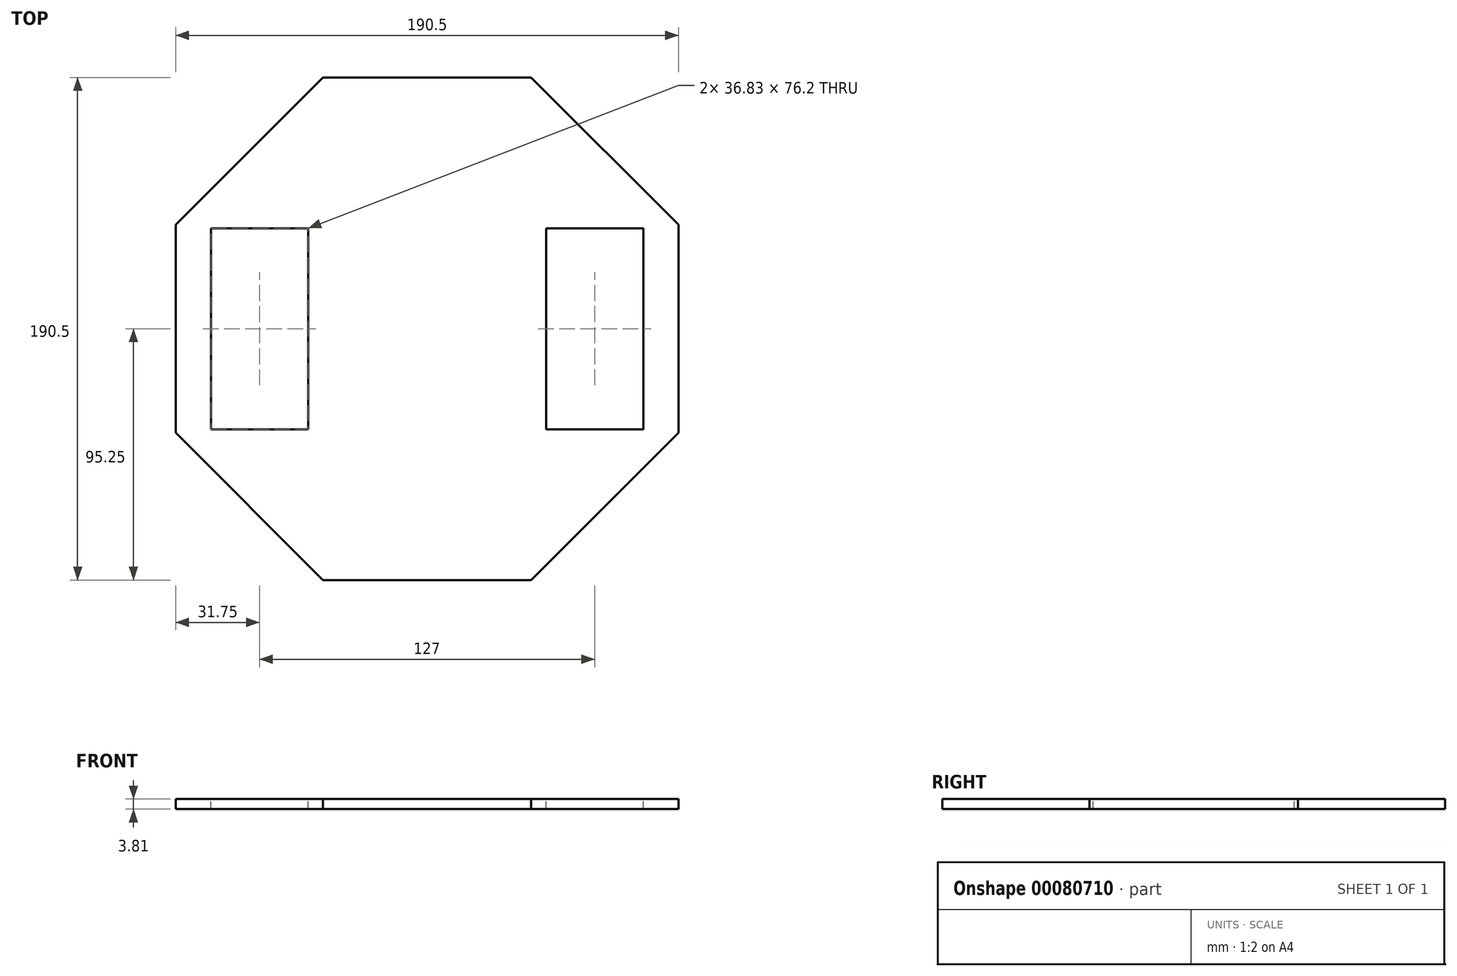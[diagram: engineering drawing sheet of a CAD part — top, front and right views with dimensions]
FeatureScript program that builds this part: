
annotation { "Feature Type Name" : "Feature", "Feature Type Description" : "" }
export const myFeature = defineFeature(function(context is Context, id is Id, definition is map)
    precondition{}
    {
        {
            var Q0;
            Q0=qCreatedBy(makeId("Top.planeOp"),FACE);
            var sketch = newSketch(context, id + "F0", { "sketchPlane" : qUnion([Q0])});
            skLineSegment(sketch, "E0.bottom", {"start": v(95.25, -39.45) * mm, "end": v(-95.25, -39.45) * mm, "construction": true});
            skLineSegment(sketch, "E0.top", {"start": v(95.25, 39.45) * mm, "end": v(-95.25, 39.45) * mm, "construction": true});
            skLineSegment(sketch, "E0.left", {"start": v(95.25, -39.45) * mm, "end": v(95.25, 39.45) * mm});
            skLineSegment(sketch, "E0.right", {"start": v(-95.25, -39.45) * mm, "end": v(-95.25, 39.45) * mm});
            skPoint(sketch, "E0.middle", {"position": v(0, 0) * mm});
            skLineSegment(sketch, "E1", {"start": v(-95.25, 39.45) * mm, "end": v(-39.45, 95.25) * mm});
            skLineSegment(sketch, "E2", {"start": v(-39.45, 95.25) * mm, "end": v(39.45, 95.25) * mm});
            skLineSegment(sketch, "E3", {"start": v(39.45, 95.25) * mm, "end": v(95.25, 39.45) * mm});
            skLineSegment(sketch, "E4", {"start": v(-95.25, -39.45) * mm, "end": v(-39.45, -95.25) * mm});
            skLineSegment(sketch, "E5", {"start": v(-39.45, -95.25) * mm, "end": v(39.45, -95.25) * mm});
            skLineSegment(sketch, "E6", {"start": v(39.45, -95.25) * mm, "end": v(95.25, -39.45) * mm});
            skLineSegment(sketch, "E7", {"start": v(0, 0) * mm, "end": v(-39.45, -95.25) * mm, "construction": true});
            skLineSegment(sketch, "E8", {"start": v(0, 0) * mm, "end": v(-95.25, -39.45) * mm, "construction": true});
            skLineSegment(sketch, "E9", {"start": v(0, 0) * mm, "end": v(39.45, -95.25) * mm, "construction": true});
            skLineSegment(sketch, "E10", {"start": v(0, 0) * mm, "end": v(95.25, -39.45) * mm, "construction": true});
            skLineSegment(sketch, "E11", {"start": v(0, 0) * mm, "end": v(95.25, 39.45) * mm, "construction": true});
            skLineSegment(sketch, "E12", {"start": v(0, 0) * mm, "end": v(39.45, 95.25) * mm, "construction": true});
            skLineSegment(sketch, "E13", {"start": v(0, 0) * mm, "end": v(-39.45, 95.25) * mm, "construction": true});
            skLineSegment(sketch, "E14", {"start": v(-95.25, 39.45) * mm, "end": v(0, 0) * mm, "construction": true});
            skSolve(sketch);
        }
        {
            var Q0;
            Q0=makeQuery(id+"F0.imprint","IMPRINT",FACE,{"disambiguationData":[TD([[makeQuery(id+"F0.imprint","IMPRINT",EDGE,{"derivedFrom":sQuery(id+"F0.wireOp",EDGE,"E0.left")}),1.0]])]});
            extrude(context, id + "F1", {"entities" : qUnion([Q0]), "depth" : 3.8 * mm});
        }
        {
            var Q0;
            Q0=makeQuery(id+"F1.opExtrude","CAP_FACE",FACE,{"disambiguationData":[OSD([sQuery(id+"F0.wireOp",EDGE,"E0.left"),sQuery(id+"F0.wireOp",EDGE,"E0.right"),sQuery(id+"F0.wireOp",EDGE,"E1"),sQuery(id+"F0.wireOp",EDGE,"E2"),sQuery(id+"F0.wireOp",EDGE,"E3"),sQuery(id+"F0.wireOp",EDGE,"E4"),sQuery(id+"F0.wireOp",EDGE,"E5"),sQuery(id+"F0.wireOp",EDGE,"E6")])],"isStart":false});
            var sketch = newSketch(context, id + "F2", { "sketchPlane" : qUnion([Q0])});
            skLineSegment(sketch, "E15.bottom", {"start": v(-45.09, -38.1) * mm, "end": v(-81.91, -38.1) * mm});
            skLineSegment(sketch, "E15.top", {"start": v(-45.09, 38.1) * mm, "end": v(-81.92, 38.1) * mm});
            skLineSegment(sketch, "E15.left", {"start": v(-45.09, -38.1) * mm, "end": v(-45.09, 38.1) * mm});
            skLineSegment(sketch, "E15.right", {"start": v(-81.92, -38.1) * mm, "end": v(-81.92, 38.1) * mm});
            skPoint(sketch, "E15.middle", {"position": v(-63.5, 0) * mm});
            skSolve(sketch);
        }
        {
            var Q0;
            Q0=makeQuery(id+"F2.imprint","IMPRINT",FACE,{"disambiguationData":[TD([[makeQuery(id+"F2.imprint","IMPRINT",EDGE,{"derivedFrom":sQuery(id+"F2.wireOp",EDGE,"E15.bottom")}),-1.0]])]});
            extrude(context, id + "F3", {"entities" : qUnion([Q0]), "operationType" : NewBodyOperationType.REMOVE, "oppositeDirection" : true, "depth" : 3.8 * mm});
        }
        {
            var Q0;
            Q0=makeQuery(id+"F1.opExtrude","SWEPT_BODY",BODY,{"disambiguationData":[OSD([sQuery(id+"F0.wireOp",EDGE,"E0.left"),sQuery(id+"F0.wireOp",EDGE,"E0.right"),sQuery(id+"F0.wireOp",EDGE,"E1"),sQuery(id+"F0.wireOp",EDGE,"E2"),sQuery(id+"F0.wireOp",EDGE,"E3"),sQuery(id+"F0.wireOp",EDGE,"E4"),sQuery(id+"F0.wireOp",EDGE,"E5"),sQuery(id+"F0.wireOp",EDGE,"E6")])]});
            var Q1;
            Q1=qCreatedBy(makeId("Right.planeOp"),FACE);
            mirror(context, id + "F4", {"operationType" : NewBodyOperationType.INTERSECT, "entities" : qUnion([Q0]), "mirrorPlane" : qUnion([Q1])});
        }
    });
